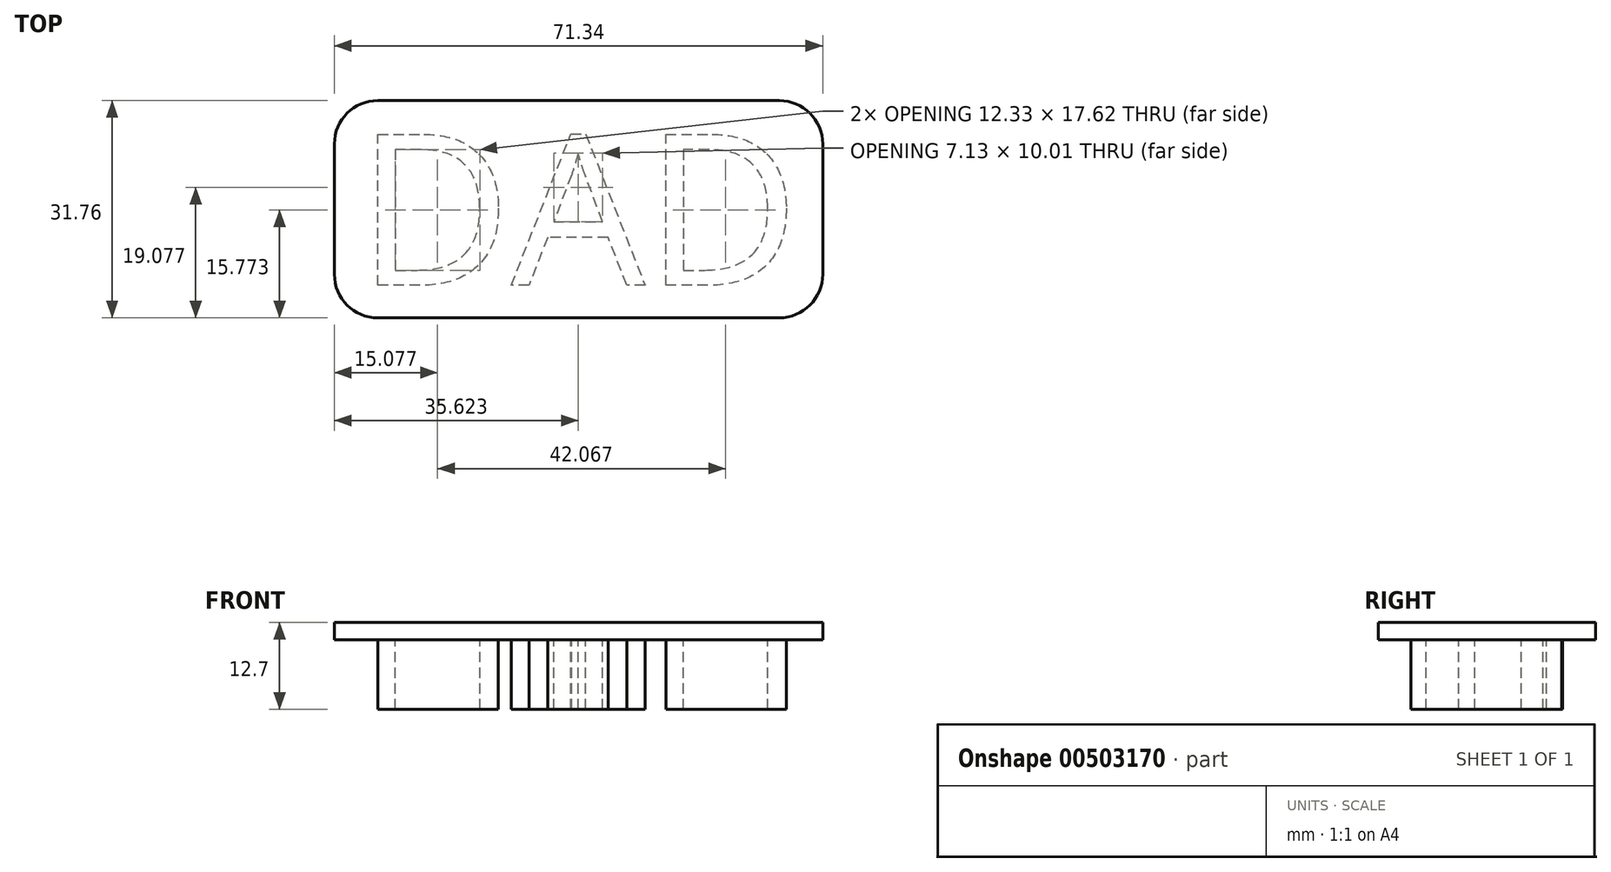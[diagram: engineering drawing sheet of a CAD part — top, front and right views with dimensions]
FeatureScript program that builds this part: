
annotation { "Feature Type Name" : "Feature", "Feature Type Description" : "" }
export const myFeature = defineFeature(function(context is Context, id is Id, definition is map)
    precondition{}
    {
        {
            var Q0;
            Q0=qCreatedBy(makeId("Top.planeOp"),FACE);
            var sketch = newSketch(context, id + "F0", { "sketchPlane" : qUnion([Q0])});
            skText(sketch, "E0", { "text": "DAD", "fontName": "OpenSans-Regular.ttf"});
            const initialGuessF0  = {"E0": [-0.03235, -0.01113, 1, 0, 0.02224]};
            skSetInitialGuess(sketch, initialGuessF0);
            skSolve(sketch);
        }
        {
            var Q0;
            Q0=qSketchRegion(id+"F0",true);
            extrude(context, id + "F1", {"entities" : qUnion([Q0]), "oppositeDirection" : true, "depth" : 10.16 * mm, "offsetDistance" : 25.4 * mm});
        }
        {
            var Q0;
            Q0=qCreatedBy(makeId("Top.planeOp"),FACE);
            var sketch = newSketch(context, id + "F2", { "sketchPlane" : qUnion([Q0])});
            skLineSegment(sketch, "E1.bottom", {"start": v(35.67, 15.88) * mm, "end": v(-35.67, 15.88) * mm});
            skLineSegment(sketch, "E1.top", {"start": v(35.67, -15.88) * mm, "end": v(-35.67, -15.88) * mm});
            skLineSegment(sketch, "E1.left", {"start": v(35.67, 15.88) * mm, "end": v(35.67, -15.87) * mm});
            skLineSegment(sketch, "E1.right", {"start": v(-35.67, 15.87) * mm, "end": v(-35.67, -15.88) * mm});
            skPoint(sketch, "E1.middle", {"position": v(0, 0) * mm});
            skSolve(sketch);
        }
        {
            var Q0;
            Q0=makeQuery(id+"F2.imprint","IMPRINT",FACE,{"disambiguationData":[TD([[makeQuery(id+"F2.imprint","IMPRINT",EDGE,{"derivedFrom":sQuery(id+"F2.wireOp",EDGE,"E1.bottom")}),1.0]])]});
            extrude(context, id + "F3", {"entities" : qUnion([Q0]), "depth" : 2.54 * mm});
        }
        {
            var Q0;
            Q0=makeQuery(id+"F3.opExtrude","SWEPT_EDGE",EDGE,{"disambiguationData":[OSD([sQuery(id+"F2.wireOp",EDGE,"E1.bottom"),sQuery(id+"F2.wireOp",EDGE,"E1.right")])]});
            var Q1;
            Q1=makeQuery(id+"F3.opExtrude","SWEPT_EDGE",EDGE,{"disambiguationData":[OSD([sQuery(id+"F2.wireOp",EDGE,"E1.top"),sQuery(id+"F2.wireOp",EDGE,"E1.right")])]});
            var Q2;
            Q2=makeQuery(id+"F3.opExtrude","SWEPT_EDGE",EDGE,{"disambiguationData":[OSD([sQuery(id+"F2.wireOp",EDGE,"E1.top"),sQuery(id+"F2.wireOp",EDGE,"E1.left")])]});
            var Q3;
            Q3=makeQuery(id+"F3.opExtrude","SWEPT_EDGE",EDGE,{"disambiguationData":[OSD([sQuery(id+"F2.wireOp",EDGE,"E1.bottom"),sQuery(id+"F2.wireOp",EDGE,"E1.left")])]});
            fillet(context, id + "F4", {"entities" : qUnion([Q0, Q1, Q2, Q3]), "radius" : 6.35 * mm, "tangentPropagation" : true, "allowEdgeOverflow" : false});
        }
    });
